# Revit family: Cabinet_Base-Cabinet_Single-Drawer_2-Doors_Moduline
name_source: partatom
category: Furniture
units: mm (PartAtom-declared; Revit-internal decimal feet)

## family parameters
Always vertical = Yes
Classification Number = 23.40.20.00
Cut with Voids When Loaded = No
Enable Cutting in Views = No
Render Appearance Source = Family Geometry
Room Calculation Point = No
Shared = No
Work Plane-Based = No

## types (12) — shared parameters
Keynote = 12 35 00
Manufacturer = Moduline Aluminum Cabinets
Model = Pro II Single Drawer Base Cabinet
Product Page URL = https://www.arcat.com
URL = https://modulinecabinets.com
zero-valued in all types: Default Elevation

## per-type parameters (varying)
| type | Depth | Description | Drawer Clearance | Handle Length | Height | Width |
| 36"H x 24"D x 36"W | 24 " | Modular Single Drawer & Double Door Base Cabinet, 36" Height x 24" Depth x 36" Width | 20.75 " | 32.5 " | 35.875 " | 36 " |
| 36"H x 24"D x 32"W | 24 " | Modular Single Drawer & Double Door Base Cabinet, 36" Height x 24" Depth x 32" Width | 20.75 " | 28.506 " | 35.875 " | 32.006 " |
| 36"H x 24"D x 30"W | 24 " | Modular Single Drawer & Double Door Base Cabinet, 36" Height x 24" Depth x 30" Width | 20.75 " | 26.5 " | 35.875 " | 30 " |
| 36"H x 18"D x 36"W | 18 " | Modular Single Drawer & Double Door Base Cabinet, 36" Height x 18" Depth x 36" Width | 14.75 " | 32.5 " | 35.875 " | 36 " |
| 36"H x 18"D x 32"W | 18 " | Modular Single Drawer & Double Door Base Cabinet, 36" Height x 18" Depth x 32" Width | 14.75 " | 28.5 " | 35.875 " | 32 " |
| 36"H x 18"D x 30"W | 18 " | Modular Single Drawer & Double Door Base Cabinet, 36" Height x 18" Depth x 30" Width | 14.75 " | 26.5 " | 35.875 " | 30 " |
| 32"H x 24"D x 36"W | 24 " | Modular Single Drawer & Double Door Base Cabinet, 32" Height x 24" Depth x 36" Width | 20.75 " | 32.5 " | 31.875 " | 36 " |
| 32"H x 24"D x 32"W | 24 " | Modular Single Drawer & Double Door Base Cabinet, 32" Height x 24" Depth x 32" Width | 20.75 " | 28.5 " | 31.875 " | 32 " |
| 32"H x 24"D x 30"W | 24 " | Modular Single Drawer & Double Door Base Cabinet, 32" Height x 24" Depth x 30" Width | 20.75 " | 26.5 " | 31.875 " | 30 " |
| 32"H x 18"D x 36"W | 18 " | Modular Single Drawer & Double Door Base Cabinet, 32" Height x 18" Depth x 36" Width | 14.75 " | 32.5 " | 31.875 " | 36 " |
| 32"H x 18"D x 32"W | 18 " | Modular Single Drawer & Double Door Base Cabinet, 32" Height x 18" Depth x 32" Width | 14.75 " | 28.5 " | 31.875 " | 32 " |
| 32"H x 18"D x 30"W | 18 " | Modular Single Drawer & Double Door Base Cabinet, 32" Height x 18" Depth x 30" Width | 14.75 " | 26.5 " | 31.875 " | 30 " |

## geometry (parser evidence)
native form markers: Sweep x6
no freeform markers — native parametric forms only
